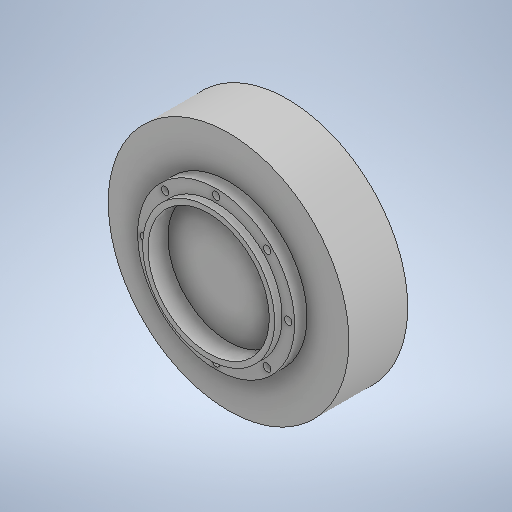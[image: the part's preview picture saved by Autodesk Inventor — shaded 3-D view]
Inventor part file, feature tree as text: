
AUTODESK INVENTOR PART (.ipt)
format: ipt  version: 2025.2 (Build 292293000, 293)  size: 281,600 bytes
history: native  units: in
note: dims shown in document units (in); Inventor stores cm internally (conversion verified against a paired STEP export)
features: extrude x1, sketch x1
ambient origin geometry x8: Origin, YZ Plane, XZ Plane, XY Plane, X Axis, Y Axis, Z Axis, Center Point
bodies: Solid1 (feature_tree), Body1 (feature_tree)
feature tree (2):
  extrude  "Extrusion1"  [1 undecoded]
  sketch  "Sketch1"  dims[d0=0.4567in d1=0.0in]
note: 1 required parameter value undecoded (feature->parameter linkage not recoverable at this tier; creation-order binding heuristic only, values carry confidence <= 0.55)
